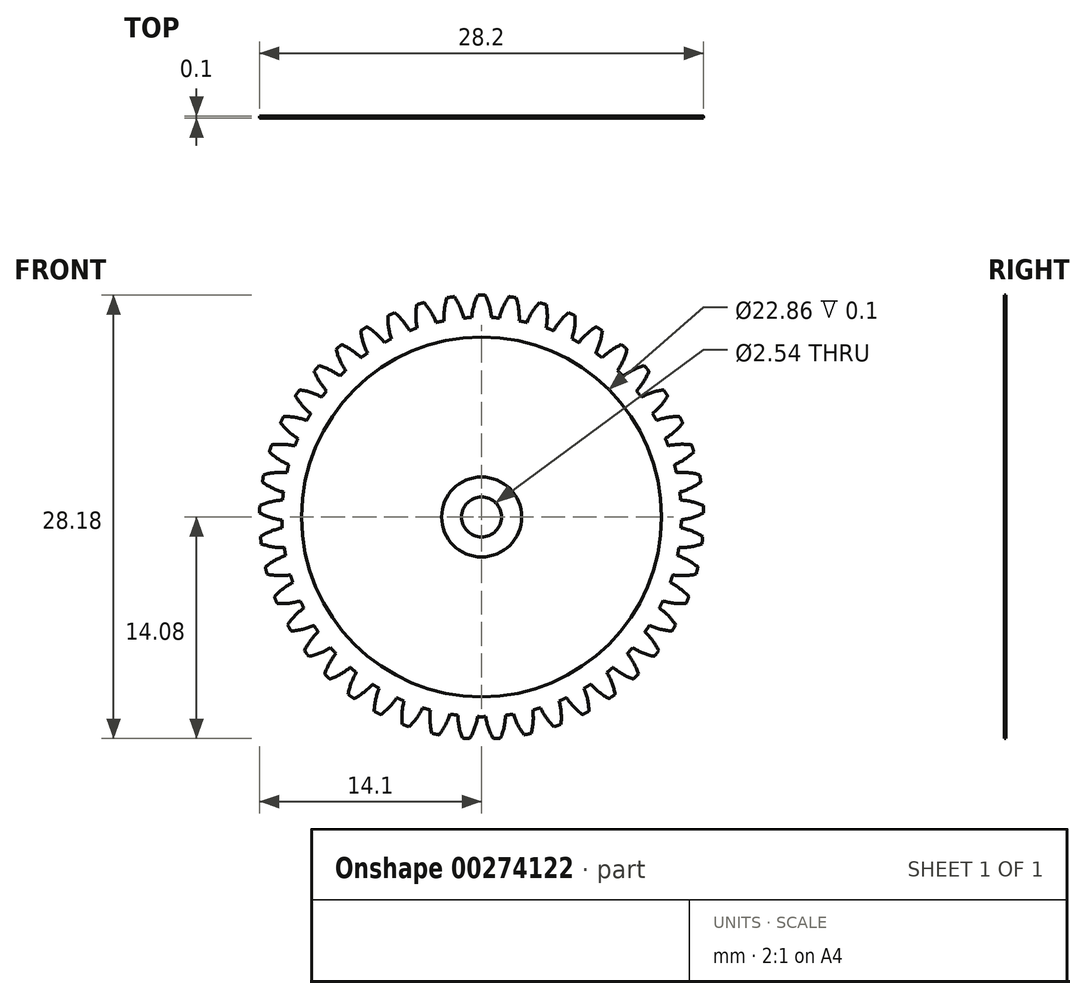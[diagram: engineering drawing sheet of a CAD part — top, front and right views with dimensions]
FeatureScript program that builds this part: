
annotation { "Feature Type Name" : "Feature", "Feature Type Description" : "" }
export const myFeature = defineFeature(function(context is Context, id is Id, definition is map)
    precondition{}
    {
        {
            assignVariable(context, id + "F0", {"name" : "teeth", "anyValue" : 45});
        }
        {
            assignVariable(context, id + "F1", {"name" : "thickness", "anyValue" : 0.1});
        }
        {
            var Q0;
            Q0=qCreatedBy(makeId("Front.planeOp"),FACE);
            var sketch = newSketch(context, id + "F2", { "sketchPlane" : qUnion([Q0])});
            skCircle(sketch, "E0", {"center": v(0, 0) * mm, "radius": 13.5 * mm, "construction": true});
            skCircle(sketch, "E1", {"center": v(0, 0) * mm, "radius": 14.1 * mm, "construction": true});
            skCircle(sketch, "E2", {"center": v(0, 0) * mm, "radius": 12.69 * mm});
            skCircle(sketch, "E3", {"center": v(27, 0) * mm, "radius": 12.69 * mm, "construction": true});
            skLineSegment(sketch, "E4", {"start": v(11.92, 4.34) * mm, "end": v(13.5, 0) * mm, "construction": true});
            skLineSegment(sketch, "E5", {"start": v(0, 0) * mm, "end": v(13.5, 0) * mm, "construction": true});
            skLineSegment(sketch, "E6", {"start": v(13.5, 0) * mm, "end": v(13.5, 28.46) * mm, "construction": true});
            skLineSegment(sketch, "E7", {"start": v(13.5, 0) * mm, "end": v(15.08, -4.34) * mm, "construction": true});
            skLineSegment(sketch, "E8", {"start": v(13.5, 0) * mm, "end": v(27, 0) * mm, "construction": true});
            skLineSegment(sketch, "E9", {"start": v(11.92, 4.34) * mm, "end": v(0, 0) * mm, "construction": true});
            skArc(sketch, "E10", {"start": v(11.92, 4.34) * mm, "mid": v(12.5, 2.1) * mm, "end": v(12.68, -0.19) * mm, "construction": true});
            skArc(sketch, "E11", {"start": v(12.68, -0.19) * mm, "mid": v(12.36, 2.86) * mm, "end": v(11.3, 5.75) * mm, "construction": true});
            skLineSegment(sketch, "E12", {"start": v(11.3, 5.75) * mm, "end": v(0, 0) * mm, "construction": true});
            skLineSegment(sketch, "E13", {"start": v(11.3, 5.75) * mm, "end": v(14.1, 0.26) * mm, "construction": true});
            skLineSegment(sketch, "E14", {"start": v(12.68, -0.19) * mm, "end": v(0, 0) * mm, "construction": true});
            skArc(sketch, "E15", {"start": v(12.68, -0.19) * mm, "mid": v(13.41, -0.03) * mm, "end": v(14.1, 0.26) * mm});
            skLineSegment(sketch, "E16", {"start": v(0, 0) * mm, "end": v(14.1, 0.5) * mm, "construction": true});
            skArc(sketch, "E17.MirrorCS", {"start": v(12.64, 1.07) * mm, "mid": v(13.38, 0.97) * mm, "end": v(14.08, 0.72) * mm});
            skPoint(sketch, "E18", {"position": v(13.47, 0.94) * mm});
            skArc(sketch, "E19", {"start": v(14.1, 0.26) * mm, "mid": v(14.1, 0.5) * mm, "end": v(14.08, 0.72) * mm});
            skPoint(sketch, "E20", {"position": v(12.68, 0.44) * mm});
            skArc(sketch, "E21", {"start": v(12.68, -0.19) * mm, "mid": v(12.68, 0.44) * mm, "end": v(12.64, 1.07) * mm});
            skCircle(sketch, "E22", {"center": v(0, 0) * mm, "radius": 1.27 * mm});
            skSolve(sketch);
        }
        {
            var Q0;
            {var subQ0=sQuery(id+"F2.wireOp",EDGE,"E2");var subQ1=makeQuery(id+"F2.imprint","INTERSECT",VERTEX,{"derivedFrom":[subQ0,sQuery(id+"F2.wireOp",EDGE,"E15")]});Q0=makeQuery(id+"F2.imprint","IMPRINT",FACE,{"disambiguationData":[TD([[makeQuery(id+"F2.imprint","IMPRINT",EDGE,{"disambiguationData":[TD([[subQ1,1.0]])],"derivedFrom":subQ0}),1.0]])]});}
            extrude(context, id + "F3", {"entities" : qUnion([Q0]), "depth" : (getVariable(context, 'thickness')) * mm});
        }
        {
            var Q0;
            {var subQ0=sQuery(id+"F2.wireOp",EDGE,"E15");Q0=makeQuery(id+"F2.imprint","IMPRINT",FACE,{"disambiguationData":[TD([[makeQuery(id+"F2.imprint","IMPRINT",EDGE,{"derivedFrom":subQ0}),1.0]])]});}
            extrude(context, id + "F4", {"entities" : qUnion([Q0]), "depth" : (getVariable(context, 'thickness')) * mm});
        }
        {
            var Q0;
            Q0=qCreatedBy(makeId("Right.planeOp"),FACE);
            var sketch = newSketch(context, id + "F5", { "sketchPlane" : qUnion([Q0])});
            skLineSegment(sketch, "E23", {"start": v(0, 0) * mm, "end": v(12.3, 0) * mm});
            skSolve(sketch);
        }
        {
            var Q0;
            Q0=makeQuery(id+"F4.opExtrude","SWEPT_BODY",BODY,{"disambiguationData":[OSD([sQuery(id+"F2.wireOp",EDGE,"E2"),sQuery(id+"F2.wireOp",EDGE,"E15"),sQuery(id+"F2.wireOp",EDGE,"E17.MirrorCS"),sQuery(id+"F2.wireOp",EDGE,"E19")])]});
            var Q1;
            Q1=sQuery(id+"F5.wireOp",EDGE,"E23");
            circularPattern(context, id + "F6", {"operationType" : NewBodyOperationType.ADD, "entities" : qUnion([Q0]), "axis" : qUnion([Q1]), "angle" : (360 / getVariable(context, 'teeth')) * degree, "instanceCount" : getVariable(context, 'teeth')});
        }
        {
            var Q0;
            {var subQ0=sQuery(id+"F2.wireOp",EDGE,"E2");var subQ1=makeQuery(id+"F4.opExtrude","CAP_FACE",FACE,{"disambiguationData":[OSD([subQ0,sQuery(id+"F2.wireOp",EDGE,"E15"),sQuery(id+"F2.wireOp",EDGE,"E17.MirrorCS"),sQuery(id+"F2.wireOp",EDGE,"E19")])],"isStart":false});Q0=makeQuery(id+"F6.boolean.opBoolean","MERGE",FACE,{"derivedFrom":[makeQuery(id+"F3.opExtrude","CAP_FACE",FACE,{"disambiguationData":[OSD([subQ0,sQuery(id+"F2.wireOp",EDGE,"E22")])],"isStart":false}),subQ1,makeQuery(id+"F6.opPattern","COPY",FACE,{"derivedFrom":subQ1,"instanceName":"1"}),makeQuery(id+"F6.opPattern","COPY",FACE,{"derivedFrom":subQ1,"instanceName":"2"}),makeQuery(id+"F6.opPattern","COPY",FACE,{"derivedFrom":subQ1,"instanceName":"3"}),makeQuery(id+"F6.opPattern","COPY",FACE,{"derivedFrom":subQ1,"instanceName":"4"}),makeQuery(id+"F6.opPattern","COPY",FACE,{"derivedFrom":subQ1,"instanceName":"5"}),makeQuery(id+"F6.opPattern","COPY",FACE,{"derivedFrom":subQ1,"instanceName":"6"}),makeQuery(id+"F6.opPattern","COPY",FACE,{"derivedFrom":subQ1,"instanceName":"7"}),makeQuery(id+"F6.opPattern","COPY",FACE,{"derivedFrom":subQ1,"instanceName":"8"}),makeQuery(id+"F6.opPattern","COPY",FACE,{"derivedFrom":subQ1,"instanceName":"9"}),makeQuery(id+"F6.opPattern","COPY",FACE,{"derivedFrom":subQ1,"instanceName":"10"}),makeQuery(id+"F6.opPattern","COPY",FACE,{"derivedFrom":subQ1,"instanceName":"11"}),makeQuery(id+"F6.opPattern","COPY",FACE,{"derivedFrom":subQ1,"instanceName":"12"}),makeQuery(id+"F6.opPattern","COPY",FACE,{"derivedFrom":subQ1,"instanceName":"13"}),makeQuery(id+"F6.opPattern","COPY",FACE,{"derivedFrom":subQ1,"instanceName":"14"}),makeQuery(id+"F6.opPattern","COPY",FACE,{"derivedFrom":subQ1,"instanceName":"15"}),makeQuery(id+"F6.opPattern","COPY",FACE,{"derivedFrom":subQ1,"instanceName":"16"}),makeQuery(id+"F6.opPattern","COPY",FACE,{"derivedFrom":subQ1,"instanceName":"17"}),makeQuery(id+"F6.opPattern","COPY",FACE,{"derivedFrom":subQ1,"instanceName":"18"}),makeQuery(id+"F6.opPattern","COPY",FACE,{"derivedFrom":subQ1,"instanceName":"19"}),makeQuery(id+"F6.opPattern","COPY",FACE,{"derivedFrom":subQ1,"instanceName":"20"}),makeQuery(id+"F6.opPattern","COPY",FACE,{"derivedFrom":subQ1,"instanceName":"21"}),makeQuery(id+"F6.opPattern","COPY",FACE,{"derivedFrom":subQ1,"instanceName":"22"}),makeQuery(id+"F6.opPattern","COPY",FACE,{"derivedFrom":subQ1,"instanceName":"23"}),makeQuery(id+"F6.opPattern","COPY",FACE,{"derivedFrom":subQ1,"instanceName":"24"}),makeQuery(id+"F6.opPattern","COPY",FACE,{"derivedFrom":subQ1,"instanceName":"25"}),makeQuery(id+"F6.opPattern","COPY",FACE,{"derivedFrom":subQ1,"instanceName":"26"}),makeQuery(id+"F6.opPattern","COPY",FACE,{"derivedFrom":subQ1,"instanceName":"27"}),makeQuery(id+"F6.opPattern","COPY",FACE,{"derivedFrom":subQ1,"instanceName":"28"}),makeQuery(id+"F6.opPattern","COPY",FACE,{"derivedFrom":subQ1,"instanceName":"29"}),makeQuery(id+"F6.opPattern","COPY",FACE,{"derivedFrom":subQ1,"instanceName":"30"}),makeQuery(id+"F6.opPattern","COPY",FACE,{"derivedFrom":subQ1,"instanceName":"31"}),makeQuery(id+"F6.opPattern","COPY",FACE,{"derivedFrom":subQ1,"instanceName":"32"}),makeQuery(id+"F6.opPattern","COPY",FACE,{"derivedFrom":subQ1,"instanceName":"33"}),makeQuery(id+"F6.opPattern","COPY",FACE,{"derivedFrom":subQ1,"instanceName":"34"}),makeQuery(id+"F6.opPattern","COPY",FACE,{"derivedFrom":subQ1,"instanceName":"35"}),makeQuery(id+"F6.opPattern","COPY",FACE,{"derivedFrom":subQ1,"instanceName":"36"}),makeQuery(id+"F6.opPattern","COPY",FACE,{"derivedFrom":subQ1,"instanceName":"37"}),makeQuery(id+"F6.opPattern","COPY",FACE,{"derivedFrom":subQ1,"instanceName":"38"}),makeQuery(id+"F6.opPattern","COPY",FACE,{"derivedFrom":subQ1,"instanceName":"39"}),makeQuery(id+"F6.opPattern","COPY",FACE,{"derivedFrom":subQ1,"instanceName":"40"}),makeQuery(id+"F6.opPattern","COPY",FACE,{"derivedFrom":subQ1,"instanceName":"41"}),makeQuery(id+"F6.opPattern","COPY",FACE,{"derivedFrom":subQ1,"instanceName":"42"}),makeQuery(id+"F6.opPattern","COPY",FACE,{"derivedFrom":subQ1,"instanceName":"43"}),makeQuery(id+"F6.opPattern","COPY",FACE,{"derivedFrom":subQ1,"instanceName":"44"})]});}
            var sketch = newSketch(context, id + "F7", { "sketchPlane" : qUnion([Q0])});
            skCircle(sketch, "E24", {"center": v(0, 0) * mm, "radius": 2.54 * mm});
            skCircle(sketch, "E25", {"center": v(0, 0) * mm, "radius": 11.43 * mm});
            skSolve(sketch);
        }
        {
            var Q0;
            Q0=qSketchRegion(id+"F7",true);
            extrude(context, id + "F8", {"entities" : qUnion([Q0]), "operationType" : NewBodyOperationType.REMOVE, "oppositeDirection" : true, "depth" : 0.64 * mm});
        }
        {
            var Q0;
            {var subQ0=sQuery(id+"F2.wireOp",EDGE,"E2");var subQ1=makeQuery(id+"F4.opExtrude","CAP_FACE",FACE,{"disambiguationData":[OSD([subQ0,sQuery(id+"F2.wireOp",EDGE,"E15"),sQuery(id+"F2.wireOp",EDGE,"E17.MirrorCS"),sQuery(id+"F2.wireOp",EDGE,"E19")])],"isStart":true});Q0=makeQuery(id+"F6.boolean.opBoolean","MERGE",FACE,{"derivedFrom":[makeQuery(id+"F3.opExtrude","CAP_FACE",FACE,{"disambiguationData":[OSD([subQ0,sQuery(id+"F2.wireOp",EDGE,"E22")])],"isStart":true}),subQ1,makeQuery(id+"F6.opPattern","COPY",FACE,{"derivedFrom":subQ1,"instanceName":"1"}),makeQuery(id+"F6.opPattern","COPY",FACE,{"derivedFrom":subQ1,"instanceName":"2"}),makeQuery(id+"F6.opPattern","COPY",FACE,{"derivedFrom":subQ1,"instanceName":"3"}),makeQuery(id+"F6.opPattern","COPY",FACE,{"derivedFrom":subQ1,"instanceName":"4"}),makeQuery(id+"F6.opPattern","COPY",FACE,{"derivedFrom":subQ1,"instanceName":"5"}),makeQuery(id+"F6.opPattern","COPY",FACE,{"derivedFrom":subQ1,"instanceName":"6"}),makeQuery(id+"F6.opPattern","COPY",FACE,{"derivedFrom":subQ1,"instanceName":"7"}),makeQuery(id+"F6.opPattern","COPY",FACE,{"derivedFrom":subQ1,"instanceName":"8"}),makeQuery(id+"F6.opPattern","COPY",FACE,{"derivedFrom":subQ1,"instanceName":"9"}),makeQuery(id+"F6.opPattern","COPY",FACE,{"derivedFrom":subQ1,"instanceName":"10"}),makeQuery(id+"F6.opPattern","COPY",FACE,{"derivedFrom":subQ1,"instanceName":"11"}),makeQuery(id+"F6.opPattern","COPY",FACE,{"derivedFrom":subQ1,"instanceName":"12"}),makeQuery(id+"F6.opPattern","COPY",FACE,{"derivedFrom":subQ1,"instanceName":"13"}),makeQuery(id+"F6.opPattern","COPY",FACE,{"derivedFrom":subQ1,"instanceName":"14"}),makeQuery(id+"F6.opPattern","COPY",FACE,{"derivedFrom":subQ1,"instanceName":"15"}),makeQuery(id+"F6.opPattern","COPY",FACE,{"derivedFrom":subQ1,"instanceName":"16"}),makeQuery(id+"F6.opPattern","COPY",FACE,{"derivedFrom":subQ1,"instanceName":"17"}),makeQuery(id+"F6.opPattern","COPY",FACE,{"derivedFrom":subQ1,"instanceName":"18"}),makeQuery(id+"F6.opPattern","COPY",FACE,{"derivedFrom":subQ1,"instanceName":"19"}),makeQuery(id+"F6.opPattern","COPY",FACE,{"derivedFrom":subQ1,"instanceName":"20"}),makeQuery(id+"F6.opPattern","COPY",FACE,{"derivedFrom":subQ1,"instanceName":"21"}),makeQuery(id+"F6.opPattern","COPY",FACE,{"derivedFrom":subQ1,"instanceName":"22"}),makeQuery(id+"F6.opPattern","COPY",FACE,{"derivedFrom":subQ1,"instanceName":"23"}),makeQuery(id+"F6.opPattern","COPY",FACE,{"derivedFrom":subQ1,"instanceName":"24"}),makeQuery(id+"F6.opPattern","COPY",FACE,{"derivedFrom":subQ1,"instanceName":"25"}),makeQuery(id+"F6.opPattern","COPY",FACE,{"derivedFrom":subQ1,"instanceName":"26"}),makeQuery(id+"F6.opPattern","COPY",FACE,{"derivedFrom":subQ1,"instanceName":"27"}),makeQuery(id+"F6.opPattern","COPY",FACE,{"derivedFrom":subQ1,"instanceName":"28"}),makeQuery(id+"F6.opPattern","COPY",FACE,{"derivedFrom":subQ1,"instanceName":"29"}),makeQuery(id+"F6.opPattern","COPY",FACE,{"derivedFrom":subQ1,"instanceName":"30"}),makeQuery(id+"F6.opPattern","COPY",FACE,{"derivedFrom":subQ1,"instanceName":"31"}),makeQuery(id+"F6.opPattern","COPY",FACE,{"derivedFrom":subQ1,"instanceName":"32"}),makeQuery(id+"F6.opPattern","COPY",FACE,{"derivedFrom":subQ1,"instanceName":"33"}),makeQuery(id+"F6.opPattern","COPY",FACE,{"derivedFrom":subQ1,"instanceName":"34"}),makeQuery(id+"F6.opPattern","COPY",FACE,{"derivedFrom":subQ1,"instanceName":"35"}),makeQuery(id+"F6.opPattern","COPY",FACE,{"derivedFrom":subQ1,"instanceName":"36"}),makeQuery(id+"F6.opPattern","COPY",FACE,{"derivedFrom":subQ1,"instanceName":"37"}),makeQuery(id+"F6.opPattern","COPY",FACE,{"derivedFrom":subQ1,"instanceName":"38"}),makeQuery(id+"F6.opPattern","COPY",FACE,{"derivedFrom":subQ1,"instanceName":"39"}),makeQuery(id+"F6.opPattern","COPY",FACE,{"derivedFrom":subQ1,"instanceName":"40"}),makeQuery(id+"F6.opPattern","COPY",FACE,{"derivedFrom":subQ1,"instanceName":"41"}),makeQuery(id+"F6.opPattern","COPY",FACE,{"derivedFrom":subQ1,"instanceName":"42"}),makeQuery(id+"F6.opPattern","COPY",FACE,{"derivedFrom":subQ1,"instanceName":"43"}),makeQuery(id+"F6.opPattern","COPY",FACE,{"derivedFrom":subQ1,"instanceName":"44"})]});}
            var sketch = newSketch(context, id + "F9", { "sketchPlane" : qUnion([Q0])});
            skCircle(sketch, "E26", {"center": v(0, 0) * mm, "radius": 2.54 * mm});
            skCircle(sketch, "E27", {"center": v(0, 0) * mm, "radius": 11.43 * mm});
            skSolve(sketch);
        }
        {
            var Q0;
            Q0=qSketchRegion(id+"F9",true);
            extrude(context, id + "F10", {"entities" : qUnion([Q0]), "operationType" : NewBodyOperationType.REMOVE, "oppositeDirection" : true, "depth" : 0.64 * mm});
        }
    });
